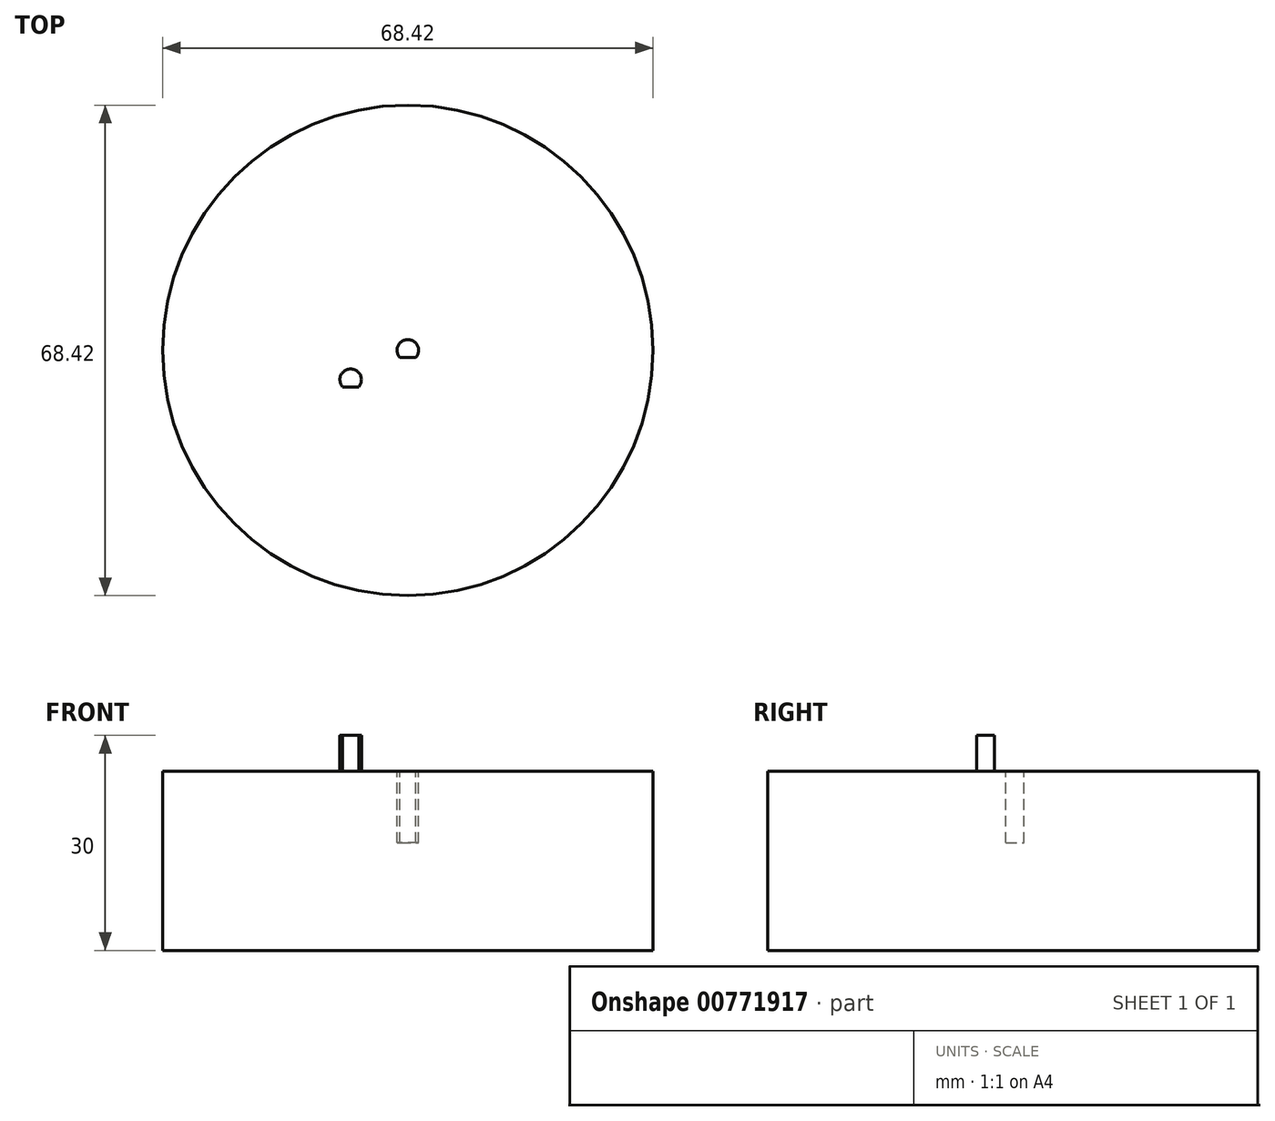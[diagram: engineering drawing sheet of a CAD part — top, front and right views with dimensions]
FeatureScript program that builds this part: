
annotation { "Feature Type Name" : "Feature", "Feature Type Description" : "" }
export const myFeature = defineFeature(function(context is Context, id is Id, definition is map)
    precondition{}
    {
        {
            var Q0;
            Q0=qCreatedBy(makeId("Top.planeOp"),FACE);
            var sketch = newSketch(context, id + "F0", { "sketchPlane" : qUnion([Q0])});
            skCircle(sketch, "E0", {"center": v(0, 0) * mm, "radius": 34.2 * mm});
            skSolve(sketch);
        }
        {
            var Q0;
            Q0 = qSketchRegion(id + "F0", true);
            extrude(context, id + "F1", {"entities" : qUnion([Q0]), "depth" : 25 * mm, "offsetDistance" : 25 * mm});
        }
        {
            var Q0;
            Q0=makeQuery(id+"F1.opExtrude","CAP_FACE",FACE,{"disambiguationData":[OSD([sQuery(id+"F0.wireOp",EDGE,"E0")])],"isStart":false});
            var sketch = newSketch(context, id + "F2", { "sketchPlane" : qUnion([Q0])});
            skArc(sketch, "E1", {"start": v(1.12, -1) * mm, "mid": v(0, 1.5) * mm, "end": v(-1.12, -1) * mm});
            skLineSegment(sketch, "E2", {"start": v(0, -1) * mm, "end": v(1.12, -1) * mm});
            skLineSegment(sketch, "E3", {"start": v(1.12, -1) * mm, "end": v(-1.12, -1) * mm});
            skPoint(sketch, "E4.orphan", {"position": v(0, 1.5) * mm});
            skSolve(sketch);
        }
        {
            var Q0;
            Q0 = qSketchRegion(id + "F2", true);
            extrude(context, id + "F3", {"entities" : qUnion([Q0]), "operationType" : NewBodyOperationType.REMOVE, "oppositeDirection" : true, "depth" : 10 * mm, "offsetDistance" : 25 * mm});
        }
        {
            var Q0;
            Q0=qCreatedBy(makeId("Top.planeOp"),FACE);
            var sketch = newSketch(context, id + "F4", { "sketchPlane" : qUnion([Q0])});
            skLineSegment(sketch, "E5.bottom", {"start": v(-2.89, -0.5) * mm, "end": v(-12.89, -0.5) * mm});
            skLineSegment(sketch, "E5.top", {"start": v(-2.89, -7.5) * mm, "end": v(-12.89, -7.5) * mm});
            skLineSegment(sketch, "E5.left", {"start": v(-2.89, -0.5) * mm, "end": v(-2.89, -7.5) * mm});
            skLineSegment(sketch, "E5.right", {"start": v(-12.89, -0.5) * mm, "end": v(-12.89, -7.5) * mm});
            skPoint(sketch, "E5.middle", {"position": v(-7.89, -4) * mm});
            skArc(sketch, "E6", {"start": v(-2.89, -0.5) * mm, "mid": v(-7.89, 2.22) * mm, "end": v(-12.89, -0.5) * mm});
            skArc(sketch, "E7", {"start": v(-12.89, -7.5) * mm, "mid": v(-7.89, -9.98) * mm, "end": v(-2.89, -7.5) * mm});
            skSolve(sketch);
        }
        {
            var Q0;
            Q0 = qSketchRegion(id + "F4", true);
            extrude(context, id + "F5", {"entities" : qUnion([Q0]), "depth" : 20 * mm, "offsetDistance" : 25 * mm});
        }
        {
            var Q0;
            Q0=makeQuery(id+"F5.opExtrude","CAP_FACE",FACE,{"disambiguationData":[OSD([sQuery(id+"F4.wireOp",EDGE,"E5.left"),sQuery(id+"F4.wireOp",EDGE,"E5.right"),sQuery(id+"F4.wireOp",EDGE,"E6"),sQuery(id+"F4.wireOp",EDGE,"E7")])],"isStart":false});
            var sketch = newSketch(context, id + "F6", { "sketchPlane" : qUnion([Q0])});
            skArc(sketch, "E8", {"start": v(-6.86, -5.1) * mm, "mid": v(-7.98, -2.6) * mm, "end": v(-9.1, -5.1) * mm});
            skLineSegment(sketch, "E9", {"start": v(-9.1, -5.1) * mm, "end": v(-7.98, -5.1) * mm});
            skLineSegment(sketch, "E10", {"start": v(-6.86, -5.1) * mm, "end": v(-7.98, -5.1) * mm});
            skSolve(sketch);
        }
        {
            var Q0;
            Q0=makeQuery(id+"F6.imprint","IMPRINT",FACE,{"disambiguationData":[TD([[makeQuery(id+"F6.imprint","IMPRINT",EDGE,{"derivedFrom":sQuery(id+"F6.wireOp",EDGE,"E8")}),1.0]])]});
            extrude(context, id + "F7", {"entities" : qUnion([Q0]), "operationType" : NewBodyOperationType.ADD, "depth" : 10 * mm, "offsetDistance" : 25 * mm});
        }
    });
